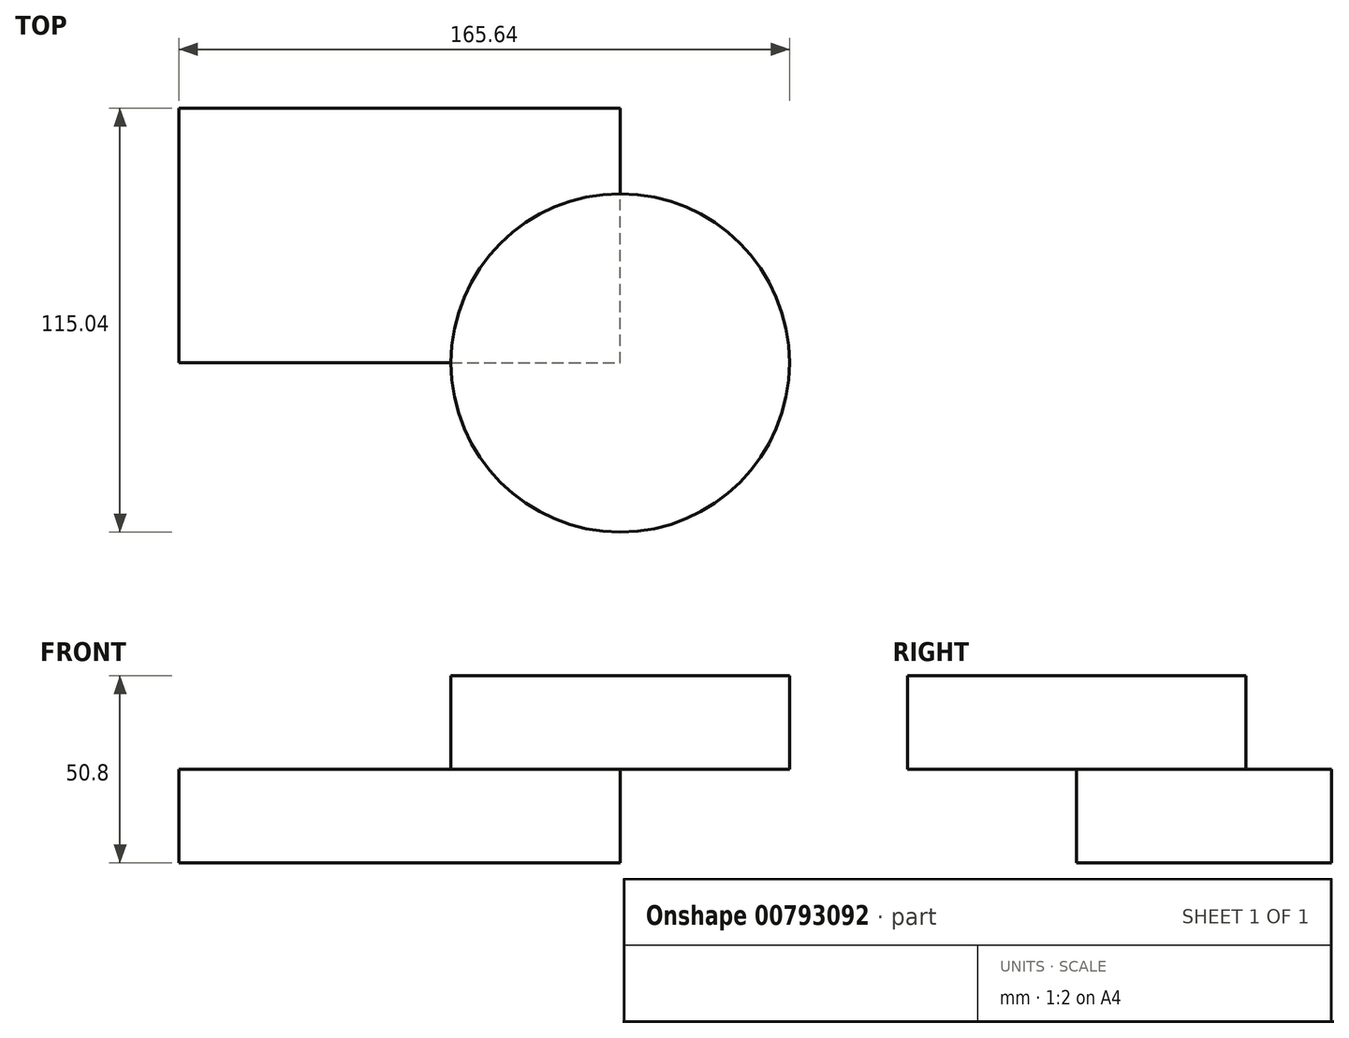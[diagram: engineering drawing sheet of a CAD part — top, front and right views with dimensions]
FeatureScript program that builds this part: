
annotation { "Feature Type Name" : "Feature", "Feature Type Description" : "" }
export const myFeature = defineFeature(function(context is Context, id is Id, definition is map)
    precondition{}
    {
        {
            var Q0;
            Q0=qCreatedBy(makeId("Top.planeOp"),FACE);
            var sketch = newSketch(context, id + "F0", { "sketchPlane" : qUnion([Q0])});
            skLineSegment(sketch, "E0.bottom", {"start": v(-55.51, -42.09) * mm, "end": v(64.2, -42.09) * mm});
            skLineSegment(sketch, "E0.top", {"start": v(-55.51, 27.03) * mm, "end": v(64.2, 27.03) * mm});
            skLineSegment(sketch, "E0.left", {"start": v(-55.51, -42.09) * mm, "end": v(-55.51, 27.03) * mm});
            skLineSegment(sketch, "E0.right", {"start": v(64.2, -42.09) * mm, "end": v(64.2, 27.03) * mm});
            skSolve(sketch);
        }
        {
            var Q0;
            Q0 = qSketchRegion(id + "F0", true);
            extrude(context, id + "F1", {"entities" : qUnion([Q0]), "depth" : 25.4 * mm, "offsetDistance" : 25.4 * mm});
        }
        {
            var Q0;
            Q0=makeQuery(id+"F1.opExtrude","CAP_FACE",FACE,{"disambiguationData":[OSD([sQuery(id+"F0.wireOp",EDGE,"E0.bottom"),sQuery(id+"F0.wireOp",EDGE,"E0.top"),sQuery(id+"F0.wireOp",EDGE,"E0.left"),sQuery(id+"F0.wireOp",EDGE,"E0.right")])],"isStart":false});
            var sketch = newSketch(context, id + "F2", { "sketchPlane" : qUnion([Q0])});
            skCircle(sketch, "E1", {"center": v(64.2, -42.09) * mm, "radius": 45.92 * mm});
            skSolve(sketch);
        }
        {
            var Q0;
            Q0 = qSketchRegion(id + "F2", true);
            extrude(context, id + "F3", {"entities" : qUnion([Q0]), "operationType" : NewBodyOperationType.ADD, "depth" : 25.4 * mm, "offsetDistance" : 25.4 * mm});
        }
        {
            var Q0;
            Q0=makeQuery(id+"F3.opExtrude","CAP_FACE",FACE,{"disambiguationData":[OSD([sQuery(id+"F2.wireOp",EDGE,"E1")])],"isStart":false});
            var sketch = newSketch(context, id + "F4", { "sketchPlane" : qUnion([Q0])});
            skCircle(sketch, "E2", {"center": v(24.64, -18.77) * mm, "radius": 27.88 * mm});
            skSolve(sketch);
        }
    });
